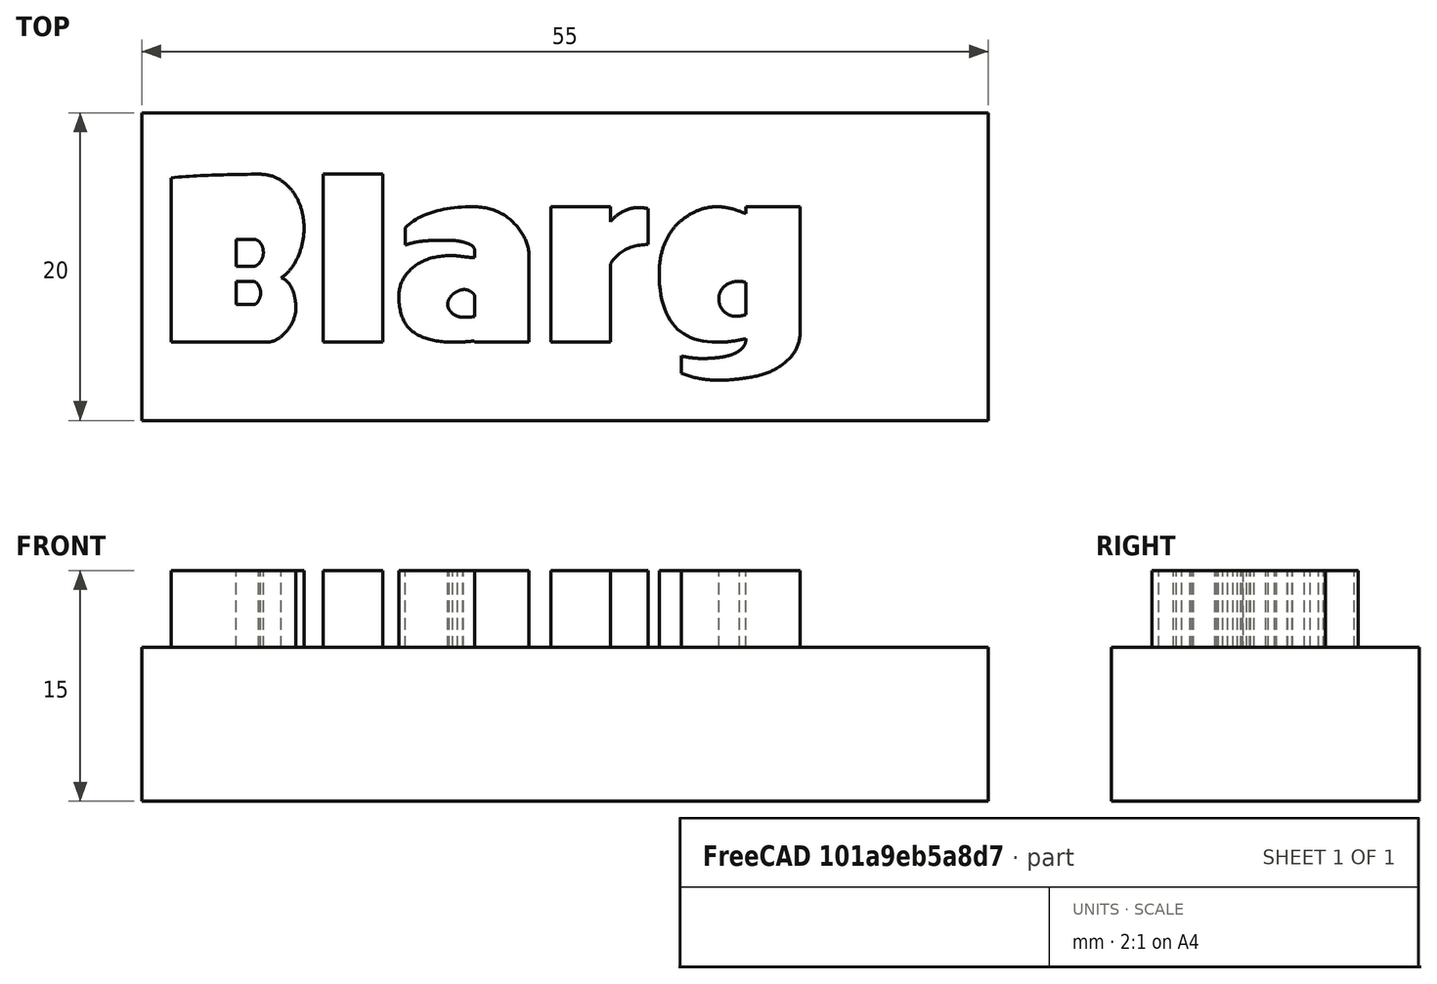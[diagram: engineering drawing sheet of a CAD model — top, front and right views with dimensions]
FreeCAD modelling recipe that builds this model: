
FCSTD DOCUMENT  (FreeCAD 0.19R)
Label: Blarg
License: All rights reserved
LicenseURL: http://en.wikipedia.org/wiki/All_rights_reserved
objects: PartDesign::Pad×2, Sketcher::SketchObject×1, Part::Part2DObjectPython×1, PartDesign::Body×1, Mesh::Feature×1
note: 7 computed .brp shape members not serialized (recipe doc carries the construction recipe); baked Part::Feature solids carry a one-line shape summary decoded from their .brp

FEATURE [Sketcher::SketchObject] Sketch
  FullyConstrained = true
  MapMode = 5
  Support = -> [XY_Plane]
  sketch-geometry (4):
    g0: LineSegment StartX=-27.5 StartY=10 StartZ=0 EndX=27.5 EndY=10 EndZ=0
    g1: LineSegment StartX=27.5 StartY=10 StartZ=0 EndX=27.5 EndY=-10 EndZ=0
    g2: LineSegment StartX=27.5 StartY=-10 StartZ=0 EndX=-27.5 EndY=-10 EndZ=0
    g3: LineSegment StartX=-27.5 StartY=-10 StartZ=0 EndX=-27.5 EndY=10 EndZ=0
  constraints (11):
    c: Coincident(g0,g1)
    c: Coincident(g1,g2)
    c: Coincident(g2,g3)
    c: Coincident(g3,g0)
    c: Horizontal(g0)
    c: Horizontal(g2)
    c: Vertical(g1)
    c: Vertical(g3)
    c: Symmetric(g1,g0,g-1)
    c: Distance(g0) = 55
    c: Distance(g1) = 20
FEATURE [PartDesign::Pad] Pad
  Direction = (1,1,1)
  Length = 10
  Length2 = 100
  Profile = -> Sketch
  Type = 0
FEATURE [Part::Part2DObjectPython] ShapeString  # Draft 2D object (typed FeaturePython)
  FontFile = <path>
  Placement = pos=(-26.3043,-4.91,10) rot=(0,0,1;0rad)
  Size = 6
  String = Blarg
  Tracking = 0
FEATURE [PartDesign::Pad] Pad001
  BaseFeature = -> Pad
  Direction = (1,1,1)
  Length = 5
  Length2 = 100
  Profile = -> ShapeString
  Type = 0
FEATURE [PartDesign::Body] Body
  Group = -> [Sketch,Pad,ShapeString,Pad001]
  Origin = -> Origin
  Tip = -> Pad001
FEATURE [Mesh::Feature] Mesh  label="Pad001 (Meshed)"
note: 1 file-system path scrubbed to <path> (originals preserved in the JSON sidecar)
